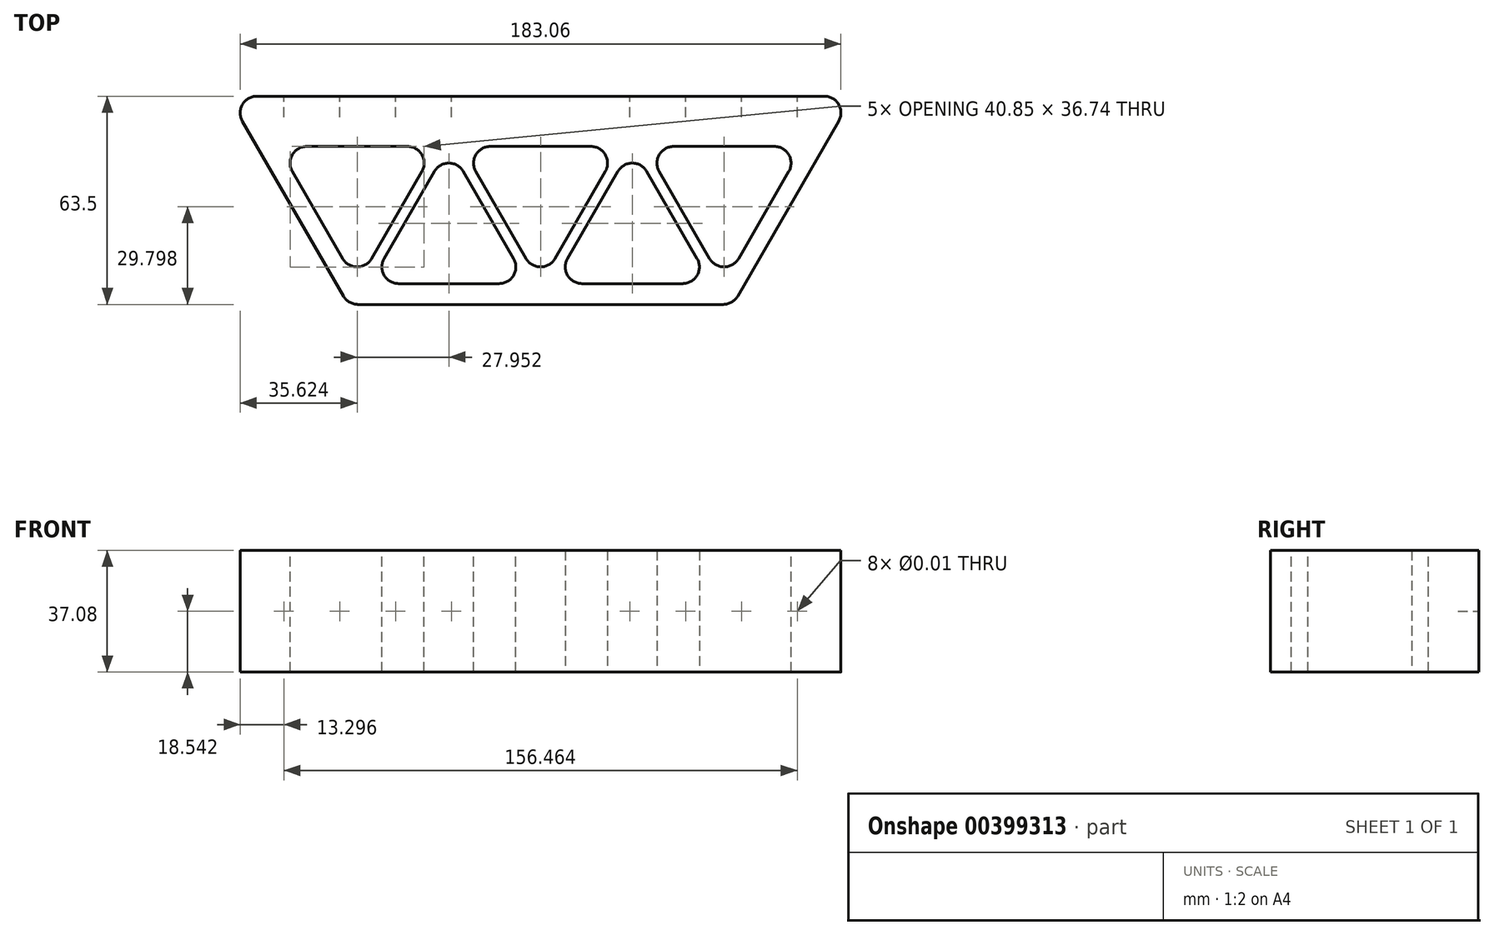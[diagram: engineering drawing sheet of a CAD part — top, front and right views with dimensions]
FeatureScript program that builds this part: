
annotation { "Feature Type Name" : "Feature", "Feature Type Description" : "" }
export const myFeature = defineFeature(function(context is Context, id is Id, definition is map)
    precondition{}
    {
        {
            var Q0;
            Q0=qCreatedBy(makeId("Top.planeOp"),FACE);
            var sketch = newSketch(context, id + "F0", { "sketchPlane" : qUnion([Q0])});
            skLineSegment(sketch, "E0", {"start": v(-36.66, 63.5) * mm, "end": v(153.84, 63.5) * mm});
            skLineSegment(sketch, "E1", {"start": v(0, 0) * mm, "end": v(117.18, 0) * mm});
            skLineSegment(sketch, "E2", {"start": v(117.18, 0) * mm, "end": v(153.84, 63.5) * mm});
            skLineSegment(sketch, "E3", {"start": v(0, 0) * mm, "end": v(-36.66, 63.5) * mm});
            skLineSegment(sketch, "E4.bottom", {"start": v(48.43, 63.5) * mm, "end": v(68.75, 63.5) * mm});
            skLineSegment(sketch, "E4.top", {"start": v(48.43, 76.2) * mm, "end": v(68.75, 76.2) * mm});
            skLineSegment(sketch, "E4.left", {"start": v(48.43, 63.5) * mm, "end": v(48.43, 76.2) * mm});
            skLineSegment(sketch, "E4.right", {"start": v(68.75, 63.5) * mm, "end": v(68.75, 76.2) * mm});
            skPoint(sketch, "E5", {"position": v(58.59, 76.2) * mm});
            skPoint(sketch, "E6", {"position": v(58.59, 0) * mm});
            skSolve(sketch);
        }
        {
            var Q0;
            Q0=makeQuery(id+"F0.imprint","IMPRINT",FACE,{"disambiguationData":[TD([[makeQuery(id+"F0.imprint","IMPRINT",EDGE,{"derivedFrom":sQuery(id+"F0.wireOp",EDGE,"E4.bottom")}),1.0]])]});
            var Q1;
            Q1=makeQuery(id+"F0.imprint","IMPRINT",FACE,{"disambiguationData":[TD([[makeQuery(id+"F0.imprint","IMPRINT",EDGE,{"derivedFrom":sQuery(id+"F0.wireOp",EDGE,"E1")}),1.0]])]});
            extrude(context, id + "F1", {"entities" : qUnion([Q0, Q1]), "depth" : 37.08 * mm});
        }
        {
            var Q0;
            {var subQ0=sQuery(id+"F0.wireOp",EDGE,"E0");Q0=makeQuery(id+"F1.opExtrude","SWEPT_FACE",FACE,{"disambiguationData":[OSD([subQ0]),TDD([makeQuery(id+"F0.imprint","IMPRINT",EDGE,{"disambiguationData":[TD([[makeQuery(id+"F0.imprint","INTERSECT",VERTEX,{"derivedFrom":[subQ0,sQuery(id+"F0.wireOp",EDGE,"E2")]}),1.0]])],"derivedFrom":subQ0})])]});}
            var sketch = newSketch(context, id + "F2", { "sketchPlane" : qUnion([Q0])});
            skPoint(sketch, "E7", {"position": v(-153.84, 18.54) * mm});
            skPoint(sketch, "E8", {"position": v(-136.82, 18.54) * mm});
            skPoint(sketch, "E9", {"position": v(-119.8, 18.54) * mm});
            skPoint(sketch, "E10", {"position": v(-102.78, 18.54) * mm});
            skPoint(sketch, "E11", {"position": v(-85.77, 18.54) * mm});
            skSolve(sketch);
        }
        {
            var Q0;
            {var subQ0=sQuery(id+"F0.wireOp",EDGE,"E0");Q0=makeQuery(id+"F1.opExtrude","SWEPT_FACE",FACE,{"disambiguationData":[OSD([subQ0]),TDD([makeQuery(id+"F0.imprint","IMPRINT",EDGE,{"disambiguationData":[TD([[makeQuery(id+"F0.imprint","INTERSECT",VERTEX,{"derivedFrom":[subQ0,sQuery(id+"F0.wireOp",EDGE,"E3")]}),-1.0]])],"derivedFrom":subQ0})])]});}
            var sketch = newSketch(context, id + "F3", { "sketchPlane" : qUnion([Q0])});
            skPoint(sketch, "E12", {"position": v(36.66, 18.54) * mm});
            skPoint(sketch, "E13", {"position": v(19.64, 18.54) * mm});
            skPoint(sketch, "E14", {"position": v(2.63, 18.54) * mm});
            skPoint(sketch, "E15", {"position": v(-14.4, 18.54) * mm});
            skPoint(sketch, "E16", {"position": v(-31.41, 18.54) * mm});
            skSolve(sketch);
        }
        {
            var Q0;
            Q0=makeQuery(id+"F1.opExtrude","SWEPT_FACE",FACE,{"disambiguationData":[OSD([sQuery(id+"F0.wireOp",EDGE,"E4.top")])]});
            var sketch = newSketch(context, id + "F4", { "sketchPlane" : qUnion([Q0])});
            skPoint(sketch, "E17", {"position": v(-68.75, 18.54) * mm});
            skPoint(sketch, "E18", {"position": v(-58.59, 18.54) * mm});
            skSolve(sketch);
        }
        {
            var Q0;
            Q0=sQuery(id+"F2.wireOp",VERTEX,"E8");
            var Q1;
            Q1=sQuery(id+"F2.wireOp",VERTEX,"E9");
            var Q2;
            Q2=sQuery(id+"F2.wireOp",VERTEX,"E10");
            var Q3;
            Q3=sQuery(id+"F2.wireOp",VERTEX,"E11");
            var Q4;
            Q4=sQuery(id+"F3.wireOp",VERTEX,"E16");
            var Q5;
            Q5=sQuery(id+"F3.wireOp",VERTEX,"E15");
            var Q6;
            Q6=sQuery(id+"F3.wireOp",VERTEX,"E14");
            var Q7;
            Q7=sQuery(id+"F3.wireOp",VERTEX,"E13");
            var Q8;
            Q8=sQuery(id+"F4.wireOp",VERTEX,"E18");
            var Q9;
            Q9=makeQuery(id+"F1.opExtrude","SWEPT_BODY",BODY,{"disambiguationData":[OSD([sQuery(id+"F0.wireOp",EDGE,"E0"),sQuery(id+"F0.wireOp",EDGE,"E1"),sQuery(id+"F0.wireOp",EDGE,"E2"),sQuery(id+"F0.wireOp",EDGE,"E3"),sQuery(id+"F0.wireOp",EDGE,"E4.top"),sQuery(id+"F0.wireOp",EDGE,"E4.left"),sQuery(id+"F0.wireOp",EDGE,"E4.right")])]});
            hole(context, id + "F5", {"style" : HoleStyle.SIMPLE, "endStyle" : HoleEndStyle.BLIND, "holeDiameter" : 3 / 203.2 * mm, "holeDepth" : 6.35 * mm, "isTappedThrough" : true, "tappedDepth" : 12.7 * mm, "tapClearance" : 3, "locations" : qUnion([Q0, Q1, Q2, Q3, Q4, Q5, Q6, Q7, Q8]), "scope" : qUnion([Q9])});
        }
        {
            var Q0;
            Q0=makeQuery(id+"F1.opExtrude","CAP_FACE",FACE,{"disambiguationData":[OSD([sQuery(id+"F0.wireOp",EDGE,"E0"),sQuery(id+"F0.wireOp",EDGE,"E1"),sQuery(id+"F0.wireOp",EDGE,"E2"),sQuery(id+"F0.wireOp",EDGE,"E3"),sQuery(id+"F0.wireOp",EDGE,"E4.top"),sQuery(id+"F0.wireOp",EDGE,"E4.left"),sQuery(id+"F0.wireOp",EDGE,"E4.right")])],"isStart":false});
            var sketch = newSketch(context, id + "F6", { "sketchPlane" : qUnion([Q0])});
            skLineSegment(sketch, "E19", {"start": v(-21.46, 48.17) * mm, "end": v(138.63, 48.17) * mm});
            skLineSegment(sketch, "E20", {"start": v(-21.46, 48.17) * mm, "end": v(2.68, 6.35) * mm});
            skLineSegment(sketch, "E21", {"start": v(2.68, 6.35) * mm, "end": v(114.5, 6.35) * mm});
            skLineSegment(sketch, "E22", {"start": v(114.5, 6.35) * mm, "end": v(138.63, 48.17) * mm});
            skPoint(sketch, "E23", {"position": v(58.59, 48.17) * mm});
            skPoint(sketch, "E24", {"position": v(58.59, 76.2) * mm});
            skPoint(sketch, "E25", {"position": v(-18.33, 31.75) * mm});
            skPoint(sketch, "E26", {"position": v(-11.98, 31.75) * mm});
            skLineSegment(sketch, "E27", {"start": v(2.68, 6.35) * mm, "end": v(26.83, 48.17) * mm});
            skLineSegment(sketch, "E28", {"start": v(6.5, 6.35) * mm, "end": v(30.64, 48.17) * mm});
            skLineSegment(sketch, "E29", {"start": v(114.5, 6.35) * mm, "end": v(90.35, 48.17) * mm});
            skLineSegment(sketch, "E30", {"start": v(110.68, 6.35) * mm, "end": v(86.54, 48.17) * mm});
            skLineSegment(sketch, "E31", {"start": v(86.54, 48.17) * mm, "end": v(62.4, 6.35) * mm});
            skLineSegment(sketch, "E32", {"start": v(82.73, 48.17) * mm, "end": v(58.59, 6.35) * mm});
            skLineSegment(sketch, "E33", {"start": v(30.64, 48.17) * mm, "end": v(54.78, 6.35) * mm});
            skLineSegment(sketch, "E34", {"start": v(34.45, 48.17) * mm, "end": v(58.59, 6.35) * mm});
            skSolve(sketch);
        }
        {
            var Q0;
            {var subQ0=sQuery(id+"F6.wireOp",EDGE,"E20");Q0=makeQuery(id+"F6.imprint","IMPRINT",FACE,{"disambiguationData":[TD([[makeQuery(id+"F6.imprint","IMPRINT",EDGE,{"derivedFrom":subQ0}),1.0]])]});}
            var Q1;
            {var subQ0=sQuery(id+"F6.wireOp",EDGE,"E28");Q1=makeQuery(id+"F6.imprint","IMPRINT",FACE,{"disambiguationData":[TD([[makeQuery(id+"F6.imprint","IMPRINT",EDGE,{"derivedFrom":subQ0}),-1.0]])]});}
            var Q2;
            {var subQ0=sQuery(id+"F6.wireOp",EDGE,"E32");Q2=makeQuery(id+"F6.imprint","IMPRINT",FACE,{"disambiguationData":[TD([[makeQuery(id+"F6.imprint","IMPRINT",EDGE,{"derivedFrom":subQ0}),-1.0]])]});}
            var Q3;
            {var subQ0=sQuery(id+"F6.wireOp",EDGE,"E30");Q3=makeQuery(id+"F6.imprint","IMPRINT",FACE,{"disambiguationData":[TD([[makeQuery(id+"F6.imprint","IMPRINT",EDGE,{"derivedFrom":subQ0}),1.0]])]});}
            var Q4;
            {var subQ0=sQuery(id+"F6.wireOp",EDGE,"E22");Q4=makeQuery(id+"F6.imprint","IMPRINT",FACE,{"disambiguationData":[TD([[makeQuery(id+"F6.imprint","IMPRINT",EDGE,{"derivedFrom":subQ0}),1.0]])]});}
            extrude(context, id + "F7", {"entities" : qUnion([Q0, Q1, Q2, Q3, Q4]), "operationType" : NewBodyOperationType.REMOVE, "endBound" : BoundingType.THROUGH_ALL, "oppositeDirection" : true, "depth" : 25.4 * mm});
        }
        {
            var Q0;
            Q0=makeQuery(id+"F1.opExtrude","SWEPT_EDGE",EDGE,{"disambiguationData":[OSD([sQuery(id+"F0.wireOp",EDGE,"E0"),sQuery(id+"F0.wireOp",EDGE,"E4.bottom"),sQuery(id+"F0.wireOp",EDGE,"E4.left")])]});
            var Q1;
            Q1=makeQuery(id+"F1.opExtrude","SWEPT_EDGE",EDGE,{"disambiguationData":[OSD([sQuery(id+"F0.wireOp",EDGE,"E0"),sQuery(id+"F0.wireOp",EDGE,"E4.bottom"),sQuery(id+"F0.wireOp",EDGE,"E4.right")])]});
            var Q2;
            Q2=makeQuery(id+"F1.opExtrude","SWEPT_EDGE",EDGE,{"disambiguationData":[OSD([sQuery(id+"F0.wireOp",EDGE,"E4.top"),sQuery(id+"F0.wireOp",EDGE,"E4.left")])]});
            var Q3;
            Q3=makeQuery(id+"F1.opExtrude","SWEPT_EDGE",EDGE,{"disambiguationData":[OSD([sQuery(id+"F0.wireOp",EDGE,"E4.top"),sQuery(id+"F0.wireOp",EDGE,"E4.right")])]});
            var Q4;
            Q4=makeQuery(id+"F1.opExtrude","SWEPT_EDGE",EDGE,{"disambiguationData":[OSD([sQuery(id+"F0.wireOp",EDGE,"E0"),sQuery(id+"F0.wireOp",EDGE,"E2")])]});
            var Q5;
            Q5=makeQuery(id+"F1.opExtrude","SWEPT_EDGE",EDGE,{"disambiguationData":[OSD([sQuery(id+"F0.wireOp",EDGE,"E0"),sQuery(id+"F0.wireOp",EDGE,"E3")])]});
            var Q6;
            Q6=makeQuery(id+"F7.boolean.opBoolean","COPY",EDGE,{"derivedFrom":makeQuery(id+"F7.opExtrude","SWEPT_EDGE",EDGE,{"disambiguationData":[OSD([sQuery(id+"F6.wireOp",EDGE,"E19"),sQuery(id+"F6.wireOp",EDGE,"E20")])]})});
            var Q7;
            Q7=makeQuery(id+"F1.opExtrude","SWEPT_EDGE",EDGE,{"disambiguationData":[OSD([sQuery(id+"F0.wireOp",EDGE,"E1"),sQuery(id+"F0.wireOp",EDGE,"E3")])]});
            var Q8;
            Q8=makeQuery(id+"F7.boolean.opBoolean","COPY",EDGE,{"derivedFrom":makeQuery(id+"F7.opExtrude","SWEPT_EDGE",EDGE,{"disambiguationData":[OSD([sQuery(id+"F6.wireOp",EDGE,"E19"),sQuery(id+"F6.wireOp",EDGE,"E27")])]})});
            var Q9;
            Q9=makeQuery(id+"F7.boolean.opBoolean","COPY",EDGE,{"derivedFrom":makeQuery(id+"F7.opExtrude","SWEPT_EDGE",EDGE,{"disambiguationData":[OSD([sQuery(id+"F6.wireOp",EDGE,"E19"),sQuery(id+"F6.wireOp",EDGE,"E32")])]})});
            var Q10;
            Q10=makeQuery(id+"F7.boolean.opBoolean","COPY",EDGE,{"derivedFrom":makeQuery(id+"F7.opExtrude","SWEPT_EDGE",EDGE,{"disambiguationData":[OSD([sQuery(id+"F6.wireOp",EDGE,"E19"),sQuery(id+"F6.wireOp",EDGE,"E22")])]})});
            var Q11;
            Q11=makeQuery(id+"F7.boolean.opBoolean","COPY",EDGE,{"derivedFrom":makeQuery(id+"F7.opExtrude","SWEPT_EDGE",EDGE,{"disambiguationData":[OSD([sQuery(id+"F6.wireOp",EDGE,"E21"),sQuery(id+"F6.wireOp",EDGE,"E30")])]})});
            var Q12;
            Q12=makeQuery(id+"F7.boolean.opBoolean","COPY",EDGE,{"derivedFrom":makeQuery(id+"F7.opExtrude","SWEPT_EDGE",EDGE,{"disambiguationData":[OSD([sQuery(id+"F6.wireOp",EDGE,"E21"),sQuery(id+"F6.wireOp",EDGE,"E22"),sQuery(id+"F6.wireOp",EDGE,"E29")])]})});
            var Q13;
            Q13=makeQuery(id+"F7.boolean.opBoolean","COPY",EDGE,{"derivedFrom":makeQuery(id+"F7.opExtrude","SWEPT_EDGE",EDGE,{"disambiguationData":[OSD([sQuery(id+"F6.wireOp",EDGE,"E20"),sQuery(id+"F6.wireOp",EDGE,"E21"),sQuery(id+"F6.wireOp",EDGE,"E27")])]})});
            var Q14;
            Q14=makeQuery(id+"F1.opExtrude","SWEPT_EDGE",EDGE,{"disambiguationData":[OSD([sQuery(id+"F0.wireOp",EDGE,"E1"),sQuery(id+"F0.wireOp",EDGE,"E2")])]});
            var Q15;
            Q15=makeQuery(id+"F7.boolean.opBoolean","COPY",EDGE,{"derivedFrom":makeQuery(id+"F7.opExtrude","SWEPT_EDGE",EDGE,{"disambiguationData":[OSD([sQuery(id+"F6.wireOp",EDGE,"E19"),sQuery(id+"F6.wireOp",EDGE,"E29")])]})});
            var Q16;
            Q16=makeQuery(id+"F7.boolean.opBoolean","COPY",EDGE,{"derivedFrom":makeQuery(id+"F7.opExtrude","SWEPT_EDGE",EDGE,{"disambiguationData":[OSD([sQuery(id+"F6.wireOp",EDGE,"E19"),sQuery(id+"F6.wireOp",EDGE,"E34")])]})});
            var Q17;
            Q17=makeQuery(id+"F7.boolean.opBoolean","COPY",EDGE,{"derivedFrom":makeQuery(id+"F7.opExtrude","SWEPT_EDGE",EDGE,{"disambiguationData":[OSD([sQuery(id+"F6.wireOp",EDGE,"E19"),sQuery(id+"F6.wireOp",EDGE,"E28"),sQuery(id+"F6.wireOp",EDGE,"E33")])]})});
            var Q18;
            Q18=makeQuery(id+"F7.boolean.opBoolean","COPY",EDGE,{"derivedFrom":makeQuery(id+"F7.opExtrude","SWEPT_EDGE",EDGE,{"disambiguationData":[OSD([sQuery(id+"F6.wireOp",EDGE,"E19"),sQuery(id+"F6.wireOp",EDGE,"E30"),sQuery(id+"F6.wireOp",EDGE,"E31")])]})});
            var Q19;
            Q19=makeQuery(id+"F7.boolean.opBoolean","COPY",EDGE,{"derivedFrom":makeQuery(id+"F7.opExtrude","SWEPT_EDGE",EDGE,{"disambiguationData":[OSD([sQuery(id+"F6.wireOp",EDGE,"E21"),sQuery(id+"F6.wireOp",EDGE,"E31")])]})});
            var Q20;
            Q20=makeQuery(id+"F7.boolean.opBoolean","COPY",EDGE,{"derivedFrom":makeQuery(id+"F7.opExtrude","SWEPT_EDGE",EDGE,{"disambiguationData":[OSD([sQuery(id+"F6.wireOp",EDGE,"E21"),sQuery(id+"F6.wireOp",EDGE,"E28")])]})});
            var Q21;
            Q21=makeQuery(id+"F7.boolean.opBoolean","COPY",EDGE,{"derivedFrom":makeQuery(id+"F7.opExtrude","SWEPT_EDGE",EDGE,{"disambiguationData":[OSD([sQuery(id+"F6.wireOp",EDGE,"E21"),sQuery(id+"F6.wireOp",EDGE,"E32"),sQuery(id+"F6.wireOp",EDGE,"E34")])]})});
            var Q22;
            Q22=makeQuery(id+"F7.boolean.opBoolean","COPY",EDGE,{"derivedFrom":makeQuery(id+"F7.opExtrude","SWEPT_EDGE",EDGE,{"disambiguationData":[OSD([sQuery(id+"F6.wireOp",EDGE,"E21"),sQuery(id+"F6.wireOp",EDGE,"E33")])]})});
            fillet(context, id + "F8", {"entities" : qUnion([Q0, Q1, Q2, Q3, Q4, Q5, Q6, Q7, Q8, Q9, Q10, Q11, Q12, Q13, Q14, Q15, Q16, Q17, Q18, Q19, Q20, Q21, Q22]), "radius" : 5.08 * mm, "tangentPropagation" : true, "allowEdgeOverflow" : false});
        }
    });
